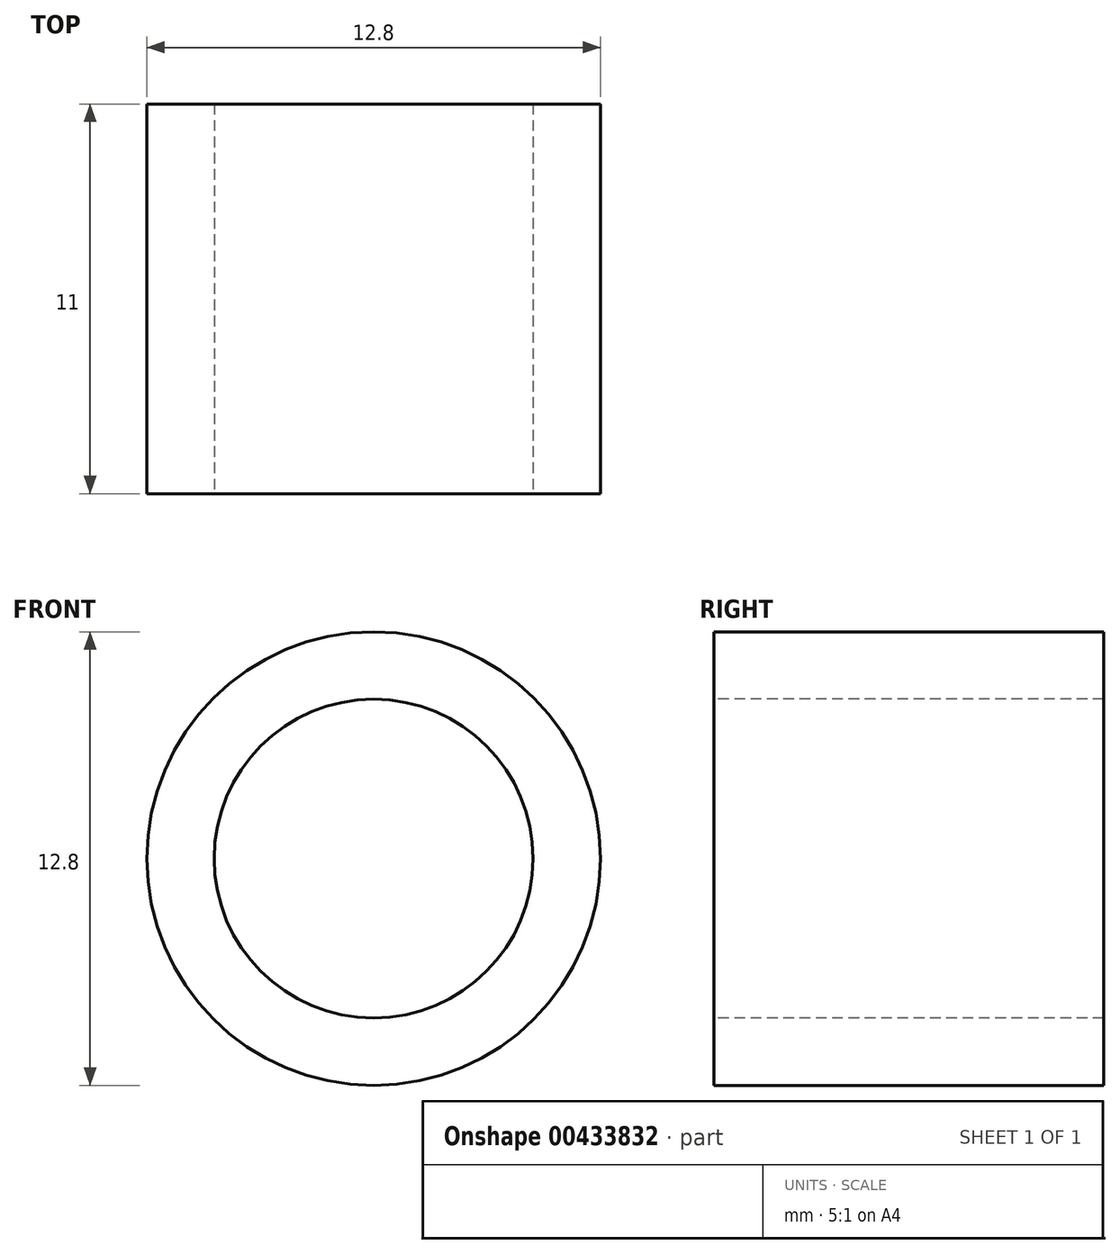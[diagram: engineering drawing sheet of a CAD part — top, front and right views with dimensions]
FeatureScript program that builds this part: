
annotation { "Feature Type Name" : "Feature", "Feature Type Description" : "" }
export const myFeature = defineFeature(function(context is Context, id is Id, definition is map)
    precondition{}
    {
        {
            var Q0;
            Q0=qCreatedBy(makeId("Front.planeOp"),FACE);
            var sketch = newSketch(context, id + "F0", { "sketchPlane" : qUnion([Q0])});
            skCircle(sketch, "E0", {"center": v(0, 0) * mm, "radius": 4.5 * mm});
            skCircle(sketch, "E1", {"center": v(0, 0) * mm, "radius": 6.4 * mm});
            skSolve(sketch);
        }
        {
            var Q0;
            Q0 = qSketchRegion(id + "F0", true);
            extrude(context, id + "F1", {"entities" : qUnion([Q0]), "oppositeDirection" : true, "depth" : 11 * mm});
        }
    });
